# Revit family: 937220001_Rejilla de Piso Clasica 10x10
name_source: partatom
category: Plumbing Fixtures
units: mm (PartAtom-declared; Revit-internal decimal feet)

## family parameters
Always vertical = Yes
Cut with Voids When Loaded = Yes
Host = Floor
OmniClass Number = 23.15.17.11.19.13
OmniClass Title = Floor Grilles
Part Type = Normal
Room Calculation Point = No
Round Connector Dimension = Use Diameter
Shared = No

## types (1)
- 937220001_Rejilla de Piso Clasica 10x10
    Alto = 99 mm
    Ancho = 99 mm
    Creado por = BIMBAU
    Default Elevation = 0 mm  [stored 0 ft]
    Description = La REJILLA PISO VANGUAR 10X10CM 11/2 -3P ha sido diseñada para trabajar en perfecta
armonía con el espacio; inspirada en las necesidades del consumidor latinoamericano
dando como resultado un producto robusto y funcional.
    Fecha de creación = 10/05/2021
    Garantía = 30 Años
    Garantía Acabados = 5 Años
    Manufacturer = Grival
    Material = Corona_Metal
    Model = Rejilla de Piso Clasica
    Peso Bruto aprox = 240gr. / 0,53Lb.
    Peso Neto aprox = 210gr. / 0,46Lb.
    Profundidad = 55 mm
    Referencia = 937200001
    Type Comments = • Fabricada en acero inoxidable.
• Cuenta con sistema anticucarachas y olores.
    URL = https://corona.co

note: [stored X ft] marks values corroborated as IEEE doubles in the binary element streams (Revit-internal decimal feet)

## geometry (parser evidence)
native form markers: Sweep x6
no freeform markers — native parametric forms only
